# Revit family: Sink-Single_Bowl-American_Standard-Portsmouth-18SB.9301800S.075
name_source: partatom
category: Plumbing Fixtures
units: mm (PartAtom-declared; Revit-internal decimal feet)

## family parameters
Always vertical = No
Cut with Voids When Loaded = Yes
OmniClass Number = 23.45.05.14.14
OmniClass Title = Sinks/Lavatories
Part Type = Normal
Room Calculation Point = No
Round Connector Dimension = Use Diameter
Shared = Yes
Work Plane-Based = Yes

## types (1)
- 18SB.9301800S.075
    9028000.075 Waste Fitting = Yes
    ASME A112.19.13 = Yes
    Assembly Code = D2010410
    Basin Shape = Rectangular
    Bowl Length = 27 3/4"
    Bowl Width = 16 1/8"
    CW Connection = Yes
    CWFU = 2
    Cold Water Connection Diameter = 1/2"
    Cold Water Connection Height = 20"
    Cold Water Connection Radius = 1/4"
    Cold Water Connection Width = 4"
    Default Elevation = 0"
    Description = Portsmouth 30 x 18 Single Bowl Stainless Steel Kitchen Sink
    Finish = Metal-American_Standard-075-Stainless_Steel
    HW Connection = No
    HWFU = 2
    Height = 9"
    Hot Water Connection Diameter = 1"
    Hot Water Connection Height = 20"
    Hot Water Connection Radius = 1/4"
    Hot Water Connection Width = 4"
    Installation Type = Undermount
    Length = 29 3/4"
    Manufacturer = American Standard
    Material = Metal-American_Standard-075-Stainless_Steel
    Model = 18SB.9301800S.075
    Price = Prices may vary. Please consult Manufacturer Representative for most up-to-date price list.
    Product Documentation Link = https://americanstandard.box.com
    Product Page URL = https://www.americanstandard-us.com
    Revised Date = 12/10/2021
    Type Comments = 36" (914mm) cabinet required
    URL = https://www.americanstandard-us.com
    Vent Connection = Yes
    WFU = 3
    Wall Distance = 3"
    Warranty Information = Limited Lifetime Warranty
    Waste Connection = Yes
    Waste Connection Diameter = 1 1/2"
    Waste Connection Height = 18"
    Waste Connection Radius = 3/4"
    Width = 18"

## geometry (parser evidence)
native form markers: Sweep x3
no freeform markers — native parametric forms only
